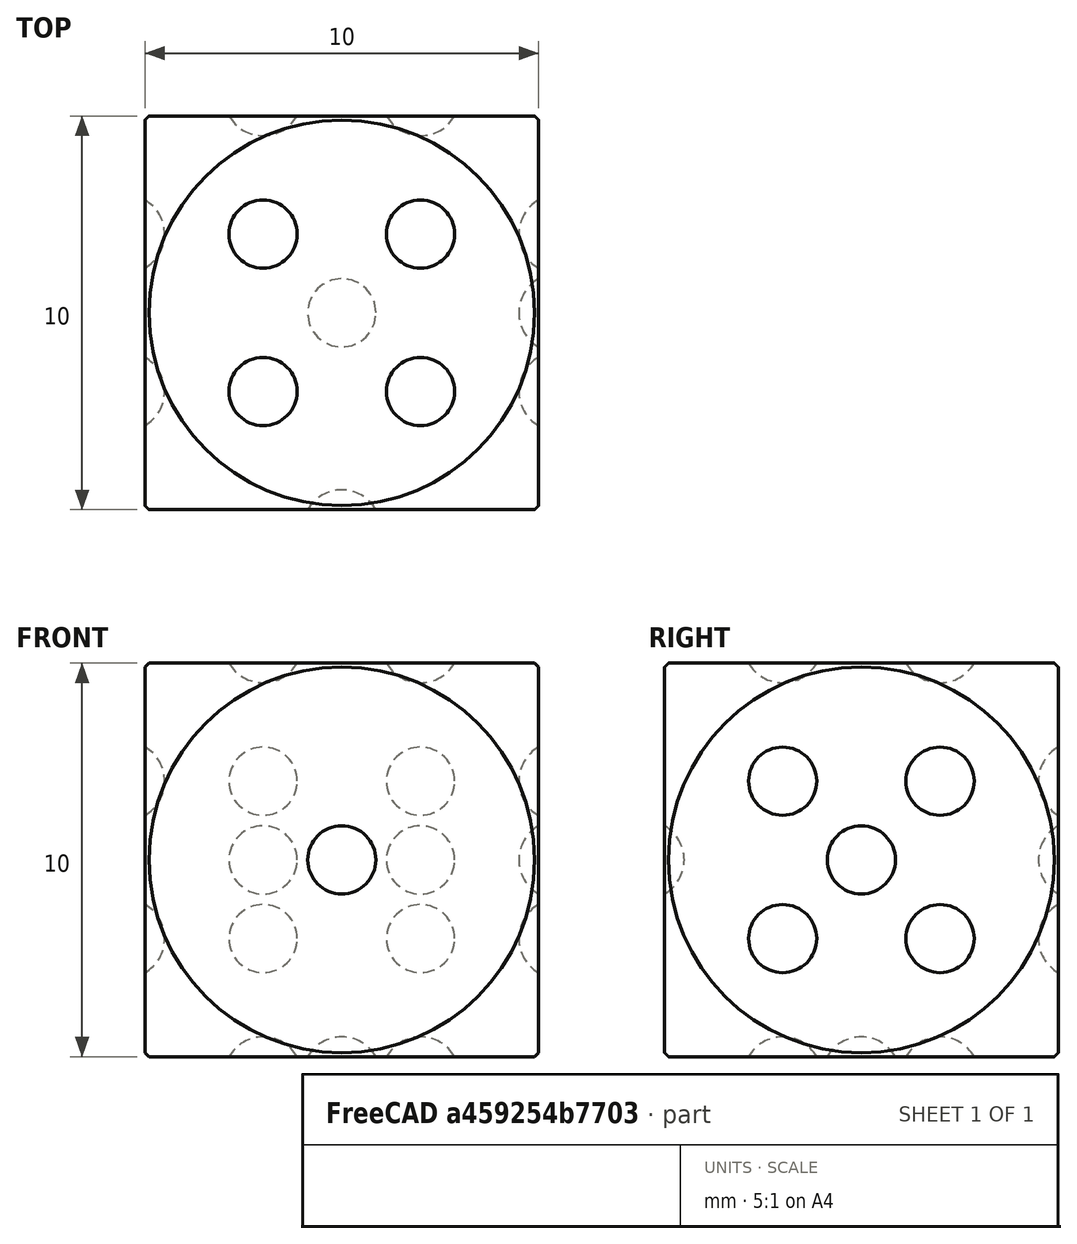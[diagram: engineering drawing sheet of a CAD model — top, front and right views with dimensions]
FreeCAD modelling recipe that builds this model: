
FCSTD DOCUMENT  (FreeCAD 0.18.1R)
Label: Dice
License: All rights reserved
LicenseURL: http://en.wikipedia.org/wiki/All_rights_reserved
objects: Part::Sphere×22, Part::MultiFuse×6, Part::Box×1, Part::MultiCommon×1, Part::Cut×1
note: 31 computed .brp shape members not serialized (recipe doc carries the construction recipe); baked Part::Feature solids carry a one-line shape summary decoded from their .brp

FEATURE [Part::Box] Box  label="Cube"
  AttacherType = Attacher::AttachEngine3D
  Height = 10
  Length = 10
  Width = 10
FEATURE [Part::Sphere] Sphere
  Angle1 = -90
  Angle2 = 90
  Angle3 = 360
  AttacherType = Attacher::AttachEngine3D
  Placement = pos=(5,5,5) rot=(0,0,1;0rad)
  Radius = 7
FEATURE [Part::MultiCommon] Common  label="BasicDice"
  Shapes = -> [Box,Sphere]
FEATURE [Part::Sphere] Sphere001  label="Side1"
  Angle1 = -90
  Angle2 = 90
  Angle3 = 360
  AttacherType = Attacher::AttachEngine3D
  Placement = pos=(5,-0.5,5) rot=(0,0,1;0rad)
  Radius = 1
FEATURE [Part::Sphere] Sphere002  label="Sphere001"
  Angle1 = -90
  Angle2 = 90
  Angle3 = 360
  AttacherType = Attacher::AttachEngine3D
  Placement = pos=(7,0,7) rot=(0,0,1;0rad)
  Radius = 1
FEATURE [Part::Sphere] Sphere003  label="Sphere002"
  Angle1 = -90
  Angle2 = 90
  Angle3 = 360
  AttacherType = Attacher::AttachEngine3D
  Placement = pos=(3,0,3) rot=(0,0,1;0rad)
  Radius = 1
FEATURE [Part::MultiFuse] Fusion  label="Side2"
  Placement = pos=(-0.5,0,0) rot=(0,0,1;1.5708rad)
  Shapes = -> [Sphere003,Sphere002]
FEATURE [Part::Sphere] Sphere004  label="Sphere003"
  Angle1 = -90
  Angle2 = 90
  Angle3 = 360
  AttacherType = Attacher::AttachEngine3D
  Placement = pos=(5,0,5) rot=(0,0,1;0rad)
  Radius = 1
FEATURE [Part::Sphere] Sphere005  label="Sphere004"
  Angle1 = -90
  Angle2 = 90
  Angle3 = 360
  AttacherType = Attacher::AttachEngine3D
  Placement = pos=(3,0,7) rot=(0,0,1;0rad)
  Radius = 1
FEATURE [Part::Sphere] Sphere006  label="Sphere005"
  Angle1 = -90
  Angle2 = 90
  Angle3 = 360
  AttacherType = Attacher::AttachEngine3D
  Placement = pos=(7,0,3) rot=(0,0,1;0rad)
  Radius = 1
FEATURE [Part::MultiFuse] Fusion001  label="Side3"
  Placement = pos=(0,0,-0.5) rot=(1,0,0;-1.5708rad)
  Shapes = -> [Sphere006,Sphere005,Sphere004]
FEATURE [Part::Sphere] Sphere007  label="Sphere006"
  Angle1 = -90
  Angle2 = 90
  Angle3 = 360
  AttacherType = Attacher::AttachEngine3D
  Placement = pos=(7,0,7) rot=(0,0,1;0rad)
  Radius = 1
FEATURE [Part::Sphere] Sphere008  label="Sphere007"
  Angle1 = -90
  Angle2 = 90
  Angle3 = 360
  AttacherType = Attacher::AttachEngine3D
  Placement = pos=(7,0,3) rot=(0,0,1;0rad)
  Radius = 1
FEATURE [Part::Sphere] Sphere009  label="Sphere008"
  Angle1 = -90
  Angle2 = 90
  Angle3 = 360
  AttacherType = Attacher::AttachEngine3D
  Placement = pos=(3,0,7) rot=(0,0,1;0rad)
  Radius = 1
FEATURE [Part::Sphere] Sphere010  label="Sphere009"
  Angle1 = -90
  Angle2 = 90
  Angle3 = 360
  AttacherType = Attacher::AttachEngine3D
  Placement = pos=(3,0,3) rot=(0,0,1;0rad)
  Radius = 1
FEATURE [Part::MultiFuse] Fusion002  label="Side4"
  Placement = pos=(0,0,10.5) rot=(1,0,0;-1.5708rad)
  Shapes = -> [Sphere010,Sphere009,Sphere008,Sphere007]
FEATURE [Part::Sphere] Sphere011  label="Sphere010"
  Angle1 = -90
  Angle2 = 90
  Angle3 = 360
  AttacherType = Attacher::AttachEngine3D
  Placement = pos=(7,0,7) rot=(0,0,1;0rad)
  Radius = 1
FEATURE [Part::Sphere] Sphere012  label="Sphere011"
  Angle1 = -90
  Angle2 = 90
  Angle3 = 360
  AttacherType = Attacher::AttachEngine3D
  Placement = pos=(7,0,3) rot=(0,0,1;0rad)
  Radius = 1
FEATURE [Part::Sphere] Sphere013  label="Sphere012"
  Angle1 = -90
  Angle2 = 90
  Angle3 = 360
  AttacherType = Attacher::AttachEngine3D
  Placement = pos=(3,0,7) rot=(0,0,1;0rad)
  Radius = 1
FEATURE [Part::Sphere] Sphere014  label="Sphere013"
  Angle1 = -90
  Angle2 = 90
  Angle3 = 360
  AttacherType = Attacher::AttachEngine3D
  Placement = pos=(3,0,3) rot=(0,0,1;0rad)
  Radius = 1
FEATURE [Part::Sphere] Sphere015  label="Sphere014"
  Angle1 = -90
  Angle2 = 90
  Angle3 = 360
  AttacherType = Attacher::AttachEngine3D
  Placement = pos=(5,0,5) rot=(0,0,1;0rad)
  Radius = 1
FEATURE [Part::MultiFuse] Fusion003  label="Side5"
  Placement = pos=(10.5,0,0) rot=(0,0,1;1.5708rad)
  Shapes = -> [Sphere015,Sphere014,Sphere013,Sphere012,Sphere011]
FEATURE [Part::Sphere] Sphere016  label="Sphere015"
  Angle1 = -90
  Angle2 = 90
  Angle3 = 360
  AttacherType = Attacher::AttachEngine3D
  Placement = pos=(7,0,7) rot=(0,0,1;0rad)
  Radius = 1
FEATURE [Part::Sphere] Sphere017  label="Sphere016"
  Angle1 = -90
  Angle2 = 90
  Angle3 = 360
  AttacherType = Attacher::AttachEngine3D
  Placement = pos=(7,0,3) rot=(0,0,1;0rad)
  Radius = 1
FEATURE [Part::Sphere] Sphere018  label="Sphere017"
  Angle1 = -90
  Angle2 = 90
  Angle3 = 360
  AttacherType = Attacher::AttachEngine3D
  Placement = pos=(3,0,7) rot=(0,0,1;0rad)
  Radius = 1
FEATURE [Part::Sphere] Sphere019  label="Sphere018"
  Angle1 = -90
  Angle2 = 90
  Angle3 = 360
  AttacherType = Attacher::AttachEngine3D
  Placement = pos=(3,0,3) rot=(0,0,1;0rad)
  Radius = 1
FEATURE [Part::Sphere] Sphere020  label="Sphere019"
  Angle1 = -90
  Angle2 = 90
  Angle3 = 360
  AttacherType = Attacher::AttachEngine3D
  Placement = pos=(3,0,5) rot=(0,0,1;0rad)
  Radius = 1
FEATURE [Part::Sphere] Sphere021  label="Sphere020"
  Angle1 = -90
  Angle2 = 90
  Angle3 = 360
  AttacherType = Attacher::AttachEngine3D
  Placement = pos=(7,0,5) rot=(0,0,1;0rad)
  Radius = 1
FEATURE [Part::MultiFuse] Fusion004  label="Side6"
  Placement = pos=(0,10.5,0) rot=(0,0,1;0rad)
  Shapes = -> [Sphere021,Sphere020,Sphere019,Sphere018,Sphere017,Sphere016]
FEATURE [Part::MultiFuse] Fusion005  label="Sides"
  Shapes = -> [Fusion004,Fusion003,Sphere001,Fusion001,Fusion002,Fusion]
FEATURE [Part::Cut] Cut  label="Dice"
  Base = -> Common
  Tool = -> Fusion005
